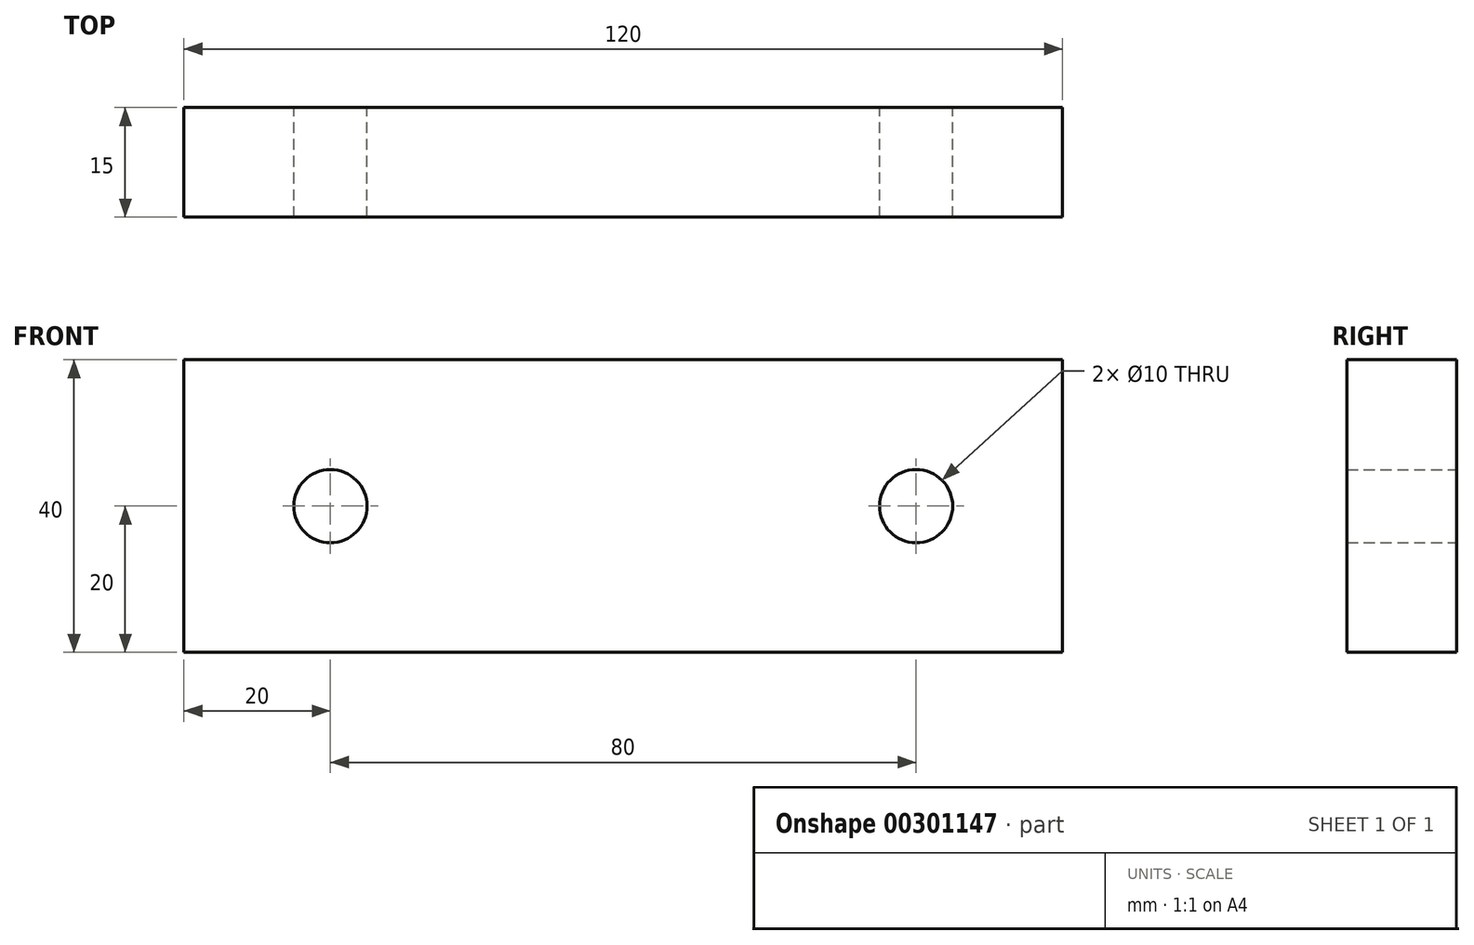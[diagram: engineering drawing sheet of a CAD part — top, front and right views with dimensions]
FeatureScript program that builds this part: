
annotation { "Feature Type Name" : "Feature", "Feature Type Description" : "" }
export const myFeature = defineFeature(function(context is Context, id is Id, definition is map)
    precondition{}
    {
        {
            var Q0;
            Q0=qCreatedBy(makeId("Front.planeOp"),FACE);
            var sketch = newSketch(context, id + "F0", { "sketchPlane" : qUnion([Q0])});
            skCircle(sketch, "E0", {"center": v(0, 0) * mm, "radius": 5 * mm});
            skLineSegment(sketch, "E1.bottom", {"start": v(-20, 20) * mm, "end": v(100, 20) * mm});
            skLineSegment(sketch, "E1.top", {"start": v(-20, -20) * mm, "end": v(100, -20) * mm});
            skLineSegment(sketch, "E1.left", {"start": v(-20, 20) * mm, "end": v(-20, -20) * mm});
            skLineSegment(sketch, "E1.right", {"start": v(100, 20) * mm, "end": v(100, -20) * mm});
            skCircle(sketch, "E2", {"center": v(80, 0) * mm, "radius": 5 * mm});
            skSolve(sketch);
        }
        {
            var Q0;
            Q0 = qSketchRegion(id + "F0", true);
            extrude(context, id + "F1", {"entities" : qUnion([Q0]), "depth" : 15 * mm});
        }
    });
